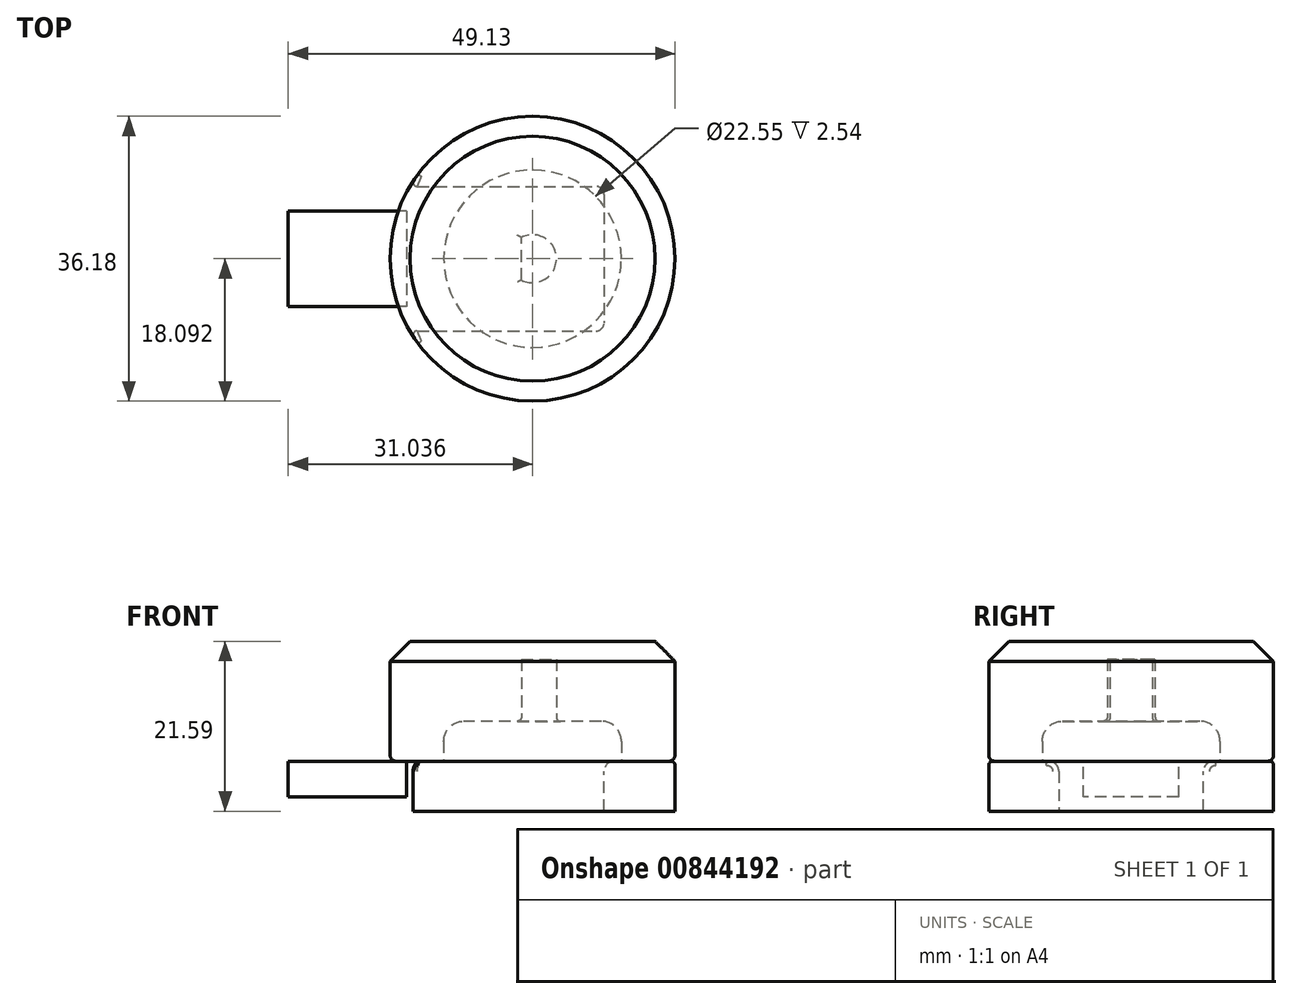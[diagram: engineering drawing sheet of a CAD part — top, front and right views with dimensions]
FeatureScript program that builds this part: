
annotation { "Feature Type Name" : "Feature", "Feature Type Description" : "" }
export const myFeature = defineFeature(function(context is Context, id is Id, definition is map)
    precondition{}
    {
        {
            var Q0;
            Q0=qCreatedBy(makeId("Top.planeOp"),FACE);
            var sketch = newSketch(context, id + "F0", { "sketchPlane" : qUnion([Q0])});
            skLineSegment(sketch, "E0.bottom", {"start": v(0, 0) * mm, "end": v(25.08, 0) * mm});
            skLineSegment(sketch, "E0.top", {"start": v(0, -18.38) * mm, "end": v(25.08, -18.38) * mm});
            skLineSegment(sketch, "E0.left", {"start": v(0, 0) * mm, "end": v(0, -18.38) * mm});
            skLineSegment(sketch, "E0.right", {"start": v(25.08, 0) * mm, "end": v(25.08, -18.38) * mm});
            skLineSegment(sketch, "E1.bottom", {"start": v(0, -3.12) * mm, "end": v(-15.04, -3.12) * mm});
            skLineSegment(sketch, "E1.top", {"start": v(0, -15.25) * mm, "end": v(-15.04, -15.25) * mm});
            skLineSegment(sketch, "E1.left", {"start": v(0, -3.12) * mm, "end": v(0, -15.25) * mm});
            skLineSegment(sketch, "E1.right", {"start": v(-15.04, -3.12) * mm, "end": v(-15.04, -15.25) * mm});
            skLineSegment(sketch, "E2", {"start": v(0, 0) * mm, "end": v(0, -3.12) * mm});
            skLineSegment(sketch, "E3", {"start": v(0, -15.25) * mm, "end": v(0, -18.38) * mm});
            skLineSegment(sketch, "E4.bottom", {"start": v(9.7, -2.46) * mm, "end": v(22.29, -2.46) * mm});
            skLineSegment(sketch, "E4.top", {"start": v(9.7, -15.91) * mm, "end": v(22.29, -15.91) * mm});
            skLineSegment(sketch, "E4.left", {"start": v(9.7, -2.46) * mm, "end": v(9.7, -15.91) * mm});
            skLineSegment(sketch, "E4.right", {"start": v(22.29, -2.46) * mm, "end": v(22.29, -15.91) * mm});
            skCircle(sketch, "E5", {"center": v(16, -9.19) * mm, "radius": 3.04 * mm});
            skLineSegment(sketch, "E6", {"start": v(16, -2.46) * mm, "end": v(16, -15.91) * mm});
            skLineSegment(sketch, "E7", {"start": v(9.7, -9.19) * mm, "end": v(22.29, -9.19) * mm});
            skLineSegment(sketch, "E8", {"start": v(16, -2.46) * mm, "end": v(16, 0) * mm});
            skLineSegment(sketch, "E9", {"start": v(16, -15.91) * mm, "end": v(16, -18.38) * mm});
            skLineSegment(sketch, "E10", {"start": v(-2.1, 18.18) * mm, "end": v(-2.1, -34.7) * mm});
            skCircle(sketch, "E11", {"center": v(16, -9.19) * mm, "radius": 18.1 * mm});
            skLineSegment(sketch, "E12", {"start": v(14.58, -6.5) * mm, "end": v(14.58, -11.88) * mm});
            skSolve(sketch);
        }
        {
            var Q0;
            {var subQ0=sQuery(id+"F0.wireOp",EDGE,"E0.right");Q0=makeQuery(id+"F0.imprint","IMPRINT",FACE,{"disambiguationData":[TD([[makeQuery(id+"F0.imprint","IMPRINT",EDGE,{"derivedFrom":subQ0}),1.0]])]});}
            extrude(context, id + "F1", {"entities" : qUnion([Q0]), "oppositeDirection" : true, "depth" : 6.35 * mm, "offsetDistance" : 25.4 * mm});
        }
        {
            var Q0;
            {var subQ4=sQuery(id+"F0.wireOp",EDGE,"E1.right");Q0=makeQuery(id+"F0.imprint","IMPRINT",FACE,{"disambiguationData":[TD([[makeQuery(id+"F0.imprint","IMPRINT",EDGE,{"derivedFrom":subQ4}),1.0]])]});}
            var Q1;
            {var subQ2=sQuery(id+"F0.wireOp",EDGE,"E1.bottom");var subQ4=sQuery(id+"F0.wireOp",EDGE,"E0.left");var subQ5=makeQuery(id+"F0.imprint","INTERSECT",VERTEX,{"derivedFrom":[subQ4,subQ2]});Q1=makeQuery(id+"F0.imprint","IMPRINT",FACE,{"disambiguationData":[TD([[makeQuery(id+"F0.imprint","IMPRINT",EDGE,{"disambiguationData":[TD([[subQ5,-1.0]])],"derivedFrom":subQ4}),-1.0]])]});}
            var Q2;
            {var subQ0=sQuery(id+"F0.wireOp",EDGE,"E10");var subQ1=sQuery(id+"F0.wireOp",EDGE,"E1.bottom");var subQ2=makeQuery(id+"F0.imprint","INTERSECT",VERTEX,{"derivedFrom":[subQ1,subQ0]});Q2=makeQuery(id+"F0.imprint","IMPRINT",FACE,{"disambiguationData":[TD([[makeQuery(id+"F0.imprint","IMPRINT",EDGE,{"disambiguationData":[TD([[subQ2,1.0]])],"derivedFrom":subQ1}),1.0]])]});}
            var Q3;
            {var subQ0=sQuery(id+"F0.wireOp",EDGE,"E10");var subQ1=sQuery(id+"F0.wireOp",EDGE,"E1.top");var subQ2=makeQuery(id+"F0.imprint","INTERSECT",VERTEX,{"derivedFrom":[subQ1,subQ0]});Q3=makeQuery(id+"F0.imprint","IMPRINT",FACE,{"disambiguationData":[TD([[makeQuery(id+"F0.imprint","IMPRINT",EDGE,{"disambiguationData":[TD([[subQ2,1.0]])],"derivedFrom":subQ1}),-1.0]])]});}
            extrude(context, id + "F2", {"entities" : qUnion([Q0, Q1, Q2, Q3]), "oppositeDirection" : true, "depth" : 4.55 * mm, "offsetDistance" : 25.4 * mm});
        }
        {
            var Q0;
            Q0=makeQuery(id+"F1.opExtrude","SWEPT_EDGE",EDGE,{"disambiguationData":[OSD([sQuery(id+"F0.wireOp",EDGE,"E0.bottom"),sQuery(id+"F0.wireOp",EDGE,"E0.right")])]});
            var Q1;
            Q1=makeQuery(id+"F1.opExtrude","SWEPT_EDGE",EDGE,{"disambiguationData":[OSD([sQuery(id+"F0.wireOp",EDGE,"E0.top"),sQuery(id+"F0.wireOp",EDGE,"E0.right")])]});
            fillet(context, id + "F3", {"entities" : qUnion([Q0, Q1]), "radius" : 1.02 * mm, "tangentPropagation" : true, "allowEdgeOverflow" : false});
        }
        {
            var Q0;
            Q0=makeQuery(id+"F1.opExtrude","CAP_EDGE",EDGE,{"disambiguationData":[OSD([sQuery(id+"F0.wireOp",EDGE,"E0.bottom")])],"isStart":true});
            fillet(context, id + "F4", {"entities" : qUnion([Q0]), "radius" : 1.27 * mm, "tangentPropagation" : true, "allowEdgeOverflow" : false});
        }
        {
            var Q0;
            Q0=qCreatedBy(makeId("Top.planeOp"),FACE);
            var sketch = newSketch(context, id + "F5", { "sketchPlane" : qUnion([Q0])});
            skCircle(sketch, "E13", {"center": v(16, -9.19) * mm, "radius": 11.28 * mm});
            skCircle(sketch, "E14", {"center": v(16, -9.19) * mm, "radius": 18.1 * mm});
            skArc(sketch, "E15", {"start": v(14.58, -11.88) * mm, "mid": v(19.04, -9.19) * mm, "end": v(14.58, -6.5) * mm});
            skLineSegment(sketch, "E16", {"start": v(14.58, -6.5) * mm, "end": v(14.58, -11.88) * mm});
            skSolve(sketch);
        }
        {
            var Q0;
            Q0=makeQuery(id+"F5.imprint","IMPRINT",FACE,{"disambiguationData":[TD([[makeQuery(id+"F5.imprint","IMPRINT",EDGE,{"derivedFrom":sQuery(id+"F5.wireOp",EDGE,"E13")}),-1.0]])]});
            var Q1;
            Q1=makeQuery(id+"F5.imprint","IMPRINT",FACE,{"disambiguationData":[TD([[makeQuery(id+"F5.imprint","IMPRINT",EDGE,{"derivedFrom":sQuery(id+"F5.wireOp",EDGE,"E13")}),1.0]])]});
            var Q2;
            Q2=makeQuery(id+"F5.imprint","IMPRINT",FACE,{"disambiguationData":[TD([[makeQuery(id+"F5.imprint","IMPRINT",EDGE,{"derivedFrom":sQuery(id+"F5.wireOp",EDGE,"E15")}),1.0]])]});
            extrude(context, id + "F6", {"entities" : qUnion([Q0, Q1, Q2]), "depth" : 15.24 * mm, "offsetDistance" : 25.4 * mm});
        }
        {
            var Q0;
            Q0=makeQuery(id+"F5.imprint","IMPRINT",FACE,{"disambiguationData":[TD([[makeQuery(id+"F5.imprint","IMPRINT",EDGE,{"derivedFrom":sQuery(id+"F5.wireOp",EDGE,"E13")}),1.0]])]});
            var Q1;
            Q1=makeQuery(id+"F5.imprint","IMPRINT",FACE,{"disambiguationData":[TD([[makeQuery(id+"F5.imprint","IMPRINT",EDGE,{"derivedFrom":sQuery(id+"F5.wireOp",EDGE,"E15")}),1.0]])]});
            var Q2;
            Q2=sQuery(id+"F5.wireOp",EDGE,"E13");
            extrude(context, id + "F7", {"entities" : qUnion([Q0, Q1]), "operationType" : NewBodyOperationType.REMOVE, "surfaceEntities" : qUnion([Q2]), "depth" : 5.08 * mm, "offsetDistance" : 25.4 * mm});
        }
        {
            var Q0;
            Q0=makeQuery(id+"F5.imprint","IMPRINT",FACE,{"disambiguationData":[TD([[makeQuery(id+"F5.imprint","IMPRINT",EDGE,{"derivedFrom":sQuery(id+"F5.wireOp",EDGE,"E15")}),1.0]])]});
            extrude(context, id + "F8", {"entities" : qUnion([Q0]), "operationType" : NewBodyOperationType.REMOVE, "depth" : 12.95 * mm, "offsetDistance" : 25.4 * mm});
        }
        {
            var Q0;
            Q0=makeQuery(id+"F6.opExtrude","CAP_EDGE",EDGE,{"disambiguationData":[OSD([sQuery(id+"F5.wireOp",EDGE,"E14")])],"isStart":false});
            chamfer(context, id + "F9", {"entities" : qUnion([Q0]), "width" : 2.54 * mm, "tangentPropagation" : true});
        }
        {
            var Q0;
            Q0=makeQuery(id+"F7.boolean.opBoolean","COPY",EDGE,{"derivedFrom":makeQuery(id+"F7.opExtrude","CAP_EDGE",EDGE,{"disambiguationData":[OSD([sQuery(id+"F5.wireOp",EDGE,"E13")])],"isStart":false})});
            fillet(context, id + "F10", {"entities" : qUnion([Q0]), "radius" : 2.54 * mm, "tangentPropagation" : true, "allowEdgeOverflow" : false});
        }
        {
            var Q0;
            Q0=makeQuery(id+"F8.boolean.opBoolean","INTERSECT",EDGE,{"derivedFrom":[makeQuery(id+"F7.boolean.opBoolean","COPY",FACE,{"derivedFrom":makeQuery(id+"F7.opExtrude","CAP_FACE",FACE,{"disambiguationData":[OSD([sQuery(id+"F5.wireOp",EDGE,"E13")])],"isStart":false})}),makeQuery(id+"F8.opExtrude","SWEPT_FACE",FACE,{"disambiguationData":[OSD([sQuery(id+"F5.wireOp",EDGE,"E15")])]})]});
            var Q1;
            Q1=makeQuery(id+"F8.boolean.opBoolean","INTERSECT",EDGE,{"derivedFrom":[makeQuery(id+"F7.boolean.opBoolean","COPY",FACE,{"derivedFrom":makeQuery(id+"F7.opExtrude","CAP_FACE",FACE,{"disambiguationData":[OSD([sQuery(id+"F5.wireOp",EDGE,"E13")])],"isStart":false})}),makeQuery(id+"F8.opExtrude","SWEPT_FACE",FACE,{"disambiguationData":[OSD([sQuery(id+"F5.wireOp",EDGE,"E16")])]})]});
            fillet(context, id + "F11", {"entities" : qUnion([Q0, Q1]), "radius" : 0.5 * mm, "tangentPropagation" : true, "allowEdgeOverflow" : false});
        }
        {
            var Q0;
            Q0=makeQuery(id+"F6.opExtrude","CAP_EDGE",EDGE,{"disambiguationData":[OSD([sQuery(id+"F5.wireOp",EDGE,"E14")])],"isStart":true});
            fillet(context, id + "F12", {"entities" : qUnion([Q0]), "radius" : 0.76 * mm, "tangentPropagation" : true, "allowEdgeOverflow" : false});
        }
        {
            var Q0;
            Q0=makeQuery(id+"F1.opExtrude","CAP_EDGE",EDGE,{"disambiguationData":[OSD([sQuery(id+"F0.wireOp",EDGE,"E11")])],"isStart":true});
            fillet(context, id + "F13", {"entities" : qUnion([Q0]), "radius" : 0.5 * mm, "tangentPropagation" : true, "allowEdgeOverflow" : false});
        }
    });
